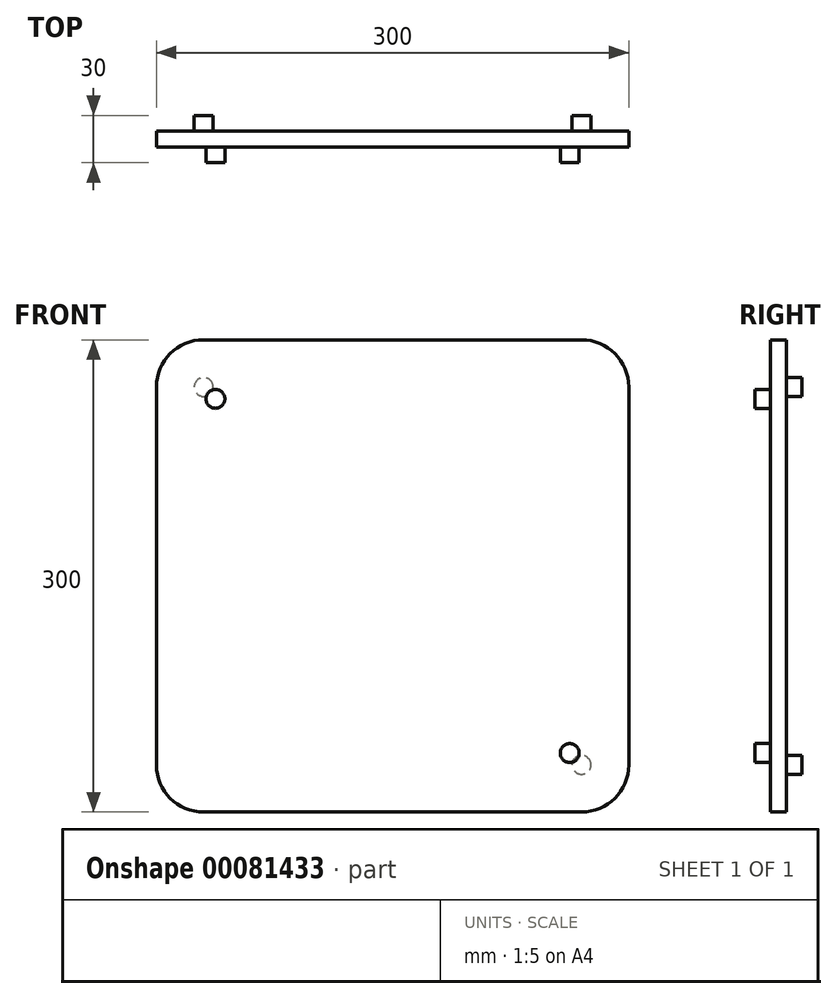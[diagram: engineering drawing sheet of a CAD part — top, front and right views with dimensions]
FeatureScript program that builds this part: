
annotation { "Feature Type Name" : "Feature", "Feature Type Description" : "" }
export const myFeature = defineFeature(function(context is Context, id is Id, definition is map)
    precondition{}
    {
        {
            var Q0;
            Q0=qCreatedBy(makeId("Front.planeOp"),FACE);
            var sketch = newSketch(context, id + "F0", { "sketchPlane" : qUnion([Q0])});
            skLineSegment(sketch, "E0.bottom", {"start": v(0, 0) * mm, "end": v(-300, 0) * mm});
            skLineSegment(sketch, "E0.top", {"start": v(0, 300) * mm, "end": v(-300, 300) * mm});
            skLineSegment(sketch, "E0.left", {"start": v(0, 0) * mm, "end": v(0, 300) * mm});
            skLineSegment(sketch, "E0.right", {"start": v(-300, 0) * mm, "end": v(-300, 300) * mm});
            skSolve(sketch);
        }
        {
            var Q0;
            Q0=makeQuery(id+"F0.imprint","IMPRINT",FACE,{"disambiguationData":[TD([[makeQuery(id+"F0.imprint","IMPRINT",EDGE,{"derivedFrom":sQuery(id+"F0.wireOp",EDGE,"E0.bottom")}),-1.0]])]});
            extrude(context, id + "F1", {"entities" : qUnion([Q0]), "depth" : 30 * mm});
        }
        {
            var Q0;
            Q0=makeQuery(id+"F1.opExtrude","SWEPT_EDGE",EDGE,{"disambiguationData":[OSD([sQuery(id+"F0.wireOp",EDGE,"E0.bottom"),sQuery(id+"F0.wireOp",EDGE,"E0.right")])]});
            var Q1;
            Q1=makeQuery(id+"F1.opExtrude","SWEPT_EDGE",EDGE,{"disambiguationData":[OSD([sQuery(id+"F0.wireOp",EDGE,"E0.bottom"),sQuery(id+"F0.wireOp",EDGE,"E0.left")])]});
            var Q2;
            Q2=makeQuery(id+"F1.opExtrude","SWEPT_EDGE",EDGE,{"disambiguationData":[OSD([sQuery(id+"F0.wireOp",EDGE,"E0.top"),sQuery(id+"F0.wireOp",EDGE,"E0.left")])]});
            var Q3;
            Q3=makeQuery(id+"F1.opExtrude","SWEPT_EDGE",EDGE,{"disambiguationData":[OSD([sQuery(id+"F0.wireOp",EDGE,"E0.top"),sQuery(id+"F0.wireOp",EDGE,"E0.right")])]});
            fillet(context, id + "F2", {"entities" : qUnion([Q0, Q1, Q2, Q3]), "radius" : 30 * mm, "tangentPropagation" : true, "allowEdgeOverflow" : false});
        }
        {
            var Q0;
            Q0=makeQuery(id+"F1.opExtrude","CAP_FACE",FACE,{"disambiguationData":[OSD([sQuery(id+"F0.wireOp",EDGE,"E0.bottom"),sQuery(id+"F0.wireOp",EDGE,"E0.top"),sQuery(id+"F0.wireOp",EDGE,"E0.left"),sQuery(id+"F0.wireOp",EDGE,"E0.right")])],"isStart":false});
            var sketch = newSketch(context, id + "F3", { "sketchPlane" : qUnion([Q0])});
            skLineSegment(sketch, "E1.0", {"start": v(-300, 30) * mm, "end": v(-300, 270) * mm});
            skLineSegment(sketch, "E1.1", {"start": v(-30, 300) * mm, "end": v(-270, 300) * mm});
            skLineSegment(sketch, "E1.2", {"start": v(-30, 0) * mm, "end": v(-270, 0) * mm});
            skLineSegment(sketch, "E1.3", {"start": v(0, 30) * mm, "end": v(0, 270) * mm});
            skArc(sketch, "E1.4", {"start": v(0, 270) * mm, "mid": v(-8.79, 291.21) * mm, "end": v(-30, 300) * mm});
            skArc(sketch, "E1.5", {"start": v(-270, 300) * mm, "mid": v(-291.21, 291.21) * mm, "end": v(-300, 270) * mm});
            skArc(sketch, "E1.6", {"start": v(-300, 30) * mm, "mid": v(-291.21, 8.79) * mm, "end": v(-270, 0) * mm});
            skArc(sketch, "E1.7", {"start": v(-30, 0) * mm, "mid": v(-8.79, 8.79) * mm, "end": v(0, 30) * mm});
            skLineSegment(sketch, "E1.8", {"start": v(-30, 300) * mm, "end": v(-270, 300) * mm});
            skLineSegment(sketch, "E2", {"start": v(-300, 150) * mm, "end": v(0, 150) * mm, "construction": true});
            skLineSegment(sketch, "E3", {"start": v(0, 150) * mm, "end": v(-150, 300) * mm, "construction": true});
            skLineSegment(sketch, "E4", {"start": v(-150, 300) * mm, "end": v(-150, 0) * mm, "construction": true});
            skCircle(sketch, "E5", {"center": v(-262.5, 37.5) * mm, "radius": 6 * mm});
            skCircle(sketch, "E6.MirrorC", {"center": v(-262.5, 262.5) * mm, "radius": 6 * mm});
            skCircle(sketch, "E7.MirrorC", {"center": v(-37.5, 37.5) * mm, "radius": 6 * mm});
            skCircle(sketch, "E8.MirrorC", {"center": v(-37.5, 262.5) * mm, "radius": 6 * mm});
            skSolve(sketch);
        }
        {
            var Q0;
            Q0=makeQuery(id+"F1.opExtrude","CAP_FACE",FACE,{"disambiguationData":[OSD([sQuery(id+"F0.wireOp",EDGE,"E0.bottom"),sQuery(id+"F0.wireOp",EDGE,"E0.top"),sQuery(id+"F0.wireOp",EDGE,"E0.left"),sQuery(id+"F0.wireOp",EDGE,"E0.right")])],"isStart":true});
            var sketch = newSketch(context, id + "F4", { "sketchPlane" : qUnion([Q0])});
            skLineSegment(sketch, "E9.0", {"start": v(300, 150) * mm, "end": v(0, 150) * mm, "construction": true});
            skLineSegment(sketch, "E9.1", {"start": v(0, 150) * mm, "end": v(150, 300) * mm, "construction": true});
            skLineSegment(sketch, "E9.2", {"start": v(150, 300) * mm, "end": v(150, 0) * mm, "construction": true});
            skLineSegment(sketch, "E9.3", {"start": v(0, 30) * mm, "end": v(0, 270) * mm});
            skLineSegment(sketch, "E9.4", {"start": v(300, 30) * mm, "end": v(300, 270) * mm});
            skLineSegment(sketch, "E9.5", {"start": v(30, 0) * mm, "end": v(270, 0) * mm});
            skLineSegment(sketch, "E9.6", {"start": v(30, 300) * mm, "end": v(270, 300) * mm});
            skCircle(sketch, "E10", {"center": v(270, 30) * mm, "radius": 6 * mm});
            skCircle(sketch, "E11.MirrorC", {"center": v(30, 30) * mm, "radius": 6 * mm});
            skCircle(sketch, "E12.MirrorC", {"center": v(30, 270) * mm, "radius": 6 * mm});
            skCircle(sketch, "E13.MirrorC", {"center": v(270, 270) * mm, "radius": 6 * mm});
            skSolve(sketch);
        }
        {
            var Q0;
            Q0=makeQuery(id+"F1.opExtrude","CAP_EDGE",EDGE,{"disambiguationData":[OSD([sQuery(id+"F0.wireOp",EDGE,"E0.right")])],"isStart":false});
            chamfer(context, id + "F5", {"entities" : qUnion([Q0]), "width" : 10 * mm, "tangentPropagation" : true});
        }
        {
            var Q0;
            Q0=makeQuery(id+"F3.imprint","IMPRINT",FACE,{"disambiguationData":[TD([[makeQuery(id+"F3.imprint","IMPRINT",EDGE,{"derivedFrom":sQuery(id+"F3.wireOp",EDGE,"E6.MirrorC")}),-1.0]])]});
            var Q1;
            Q1=makeQuery(id+"F3.imprint","IMPRINT",FACE,{"disambiguationData":[TD([[makeQuery(id+"F3.imprint","IMPRINT",EDGE,{"derivedFrom":sQuery(id+"F3.wireOp",EDGE,"E5")}),1.0]])]});
            var Q2;
            Q2=makeQuery(id+"F3.imprint","IMPRINT",FACE,{"disambiguationData":[TD([[makeQuery(id+"F3.imprint","IMPRINT",EDGE,{"derivedFrom":sQuery(id+"F3.wireOp",EDGE,"E7.MirrorC")}),-1.0]])]});
            var Q3;
            Q3=makeQuery(id+"F3.imprint","IMPRINT",FACE,{"disambiguationData":[TD([[makeQuery(id+"F3.imprint","IMPRINT",EDGE,{"derivedFrom":sQuery(id+"F3.wireOp",EDGE,"E8.MirrorC")}),1.0]])]});
            var Q4;
            Q4=makeQuery(id+"F4.imprint","IMPRINT",FACE,{"disambiguationData":[TD([[makeQuery(id+"F4.imprint","IMPRINT",EDGE,{"derivedFrom":sQuery(id+"F4.wireOp",EDGE,"E12.MirrorC")}),1.0]])]});
            var Q5;
            Q5=makeQuery(id+"F4.imprint","IMPRINT",FACE,{"disambiguationData":[TD([[makeQuery(id+"F4.imprint","IMPRINT",EDGE,{"derivedFrom":sQuery(id+"F4.wireOp",EDGE,"E13.MirrorC")}),-1.0]])]});
            var Q6;
            Q6=makeQuery(id+"F4.imprint","IMPRINT",FACE,{"disambiguationData":[TD([[makeQuery(id+"F4.imprint","IMPRINT",EDGE,{"derivedFrom":sQuery(id+"F4.wireOp",EDGE,"E10")}),1.0]])]});
            var Q7;
            Q7=makeQuery(id+"F4.imprint","IMPRINT",FACE,{"disambiguationData":[TD([[makeQuery(id+"F4.imprint","IMPRINT",EDGE,{"derivedFrom":sQuery(id+"F4.wireOp",EDGE,"E11.MirrorC")}),-1.0]])]});
            extrude(context, id + "F6", {"entities" : qUnion([Q0, Q1, Q2, Q3, Q4, Q5, Q6, Q7]), "operationType" : NewBodyOperationType.REMOVE, "oppositeDirection" : true, "depth" : 10 * mm});
        }
        {
            var Q0;
            Q0=makeQuery(id+"F4.imprint","IMPRINT",FACE,{"disambiguationData":[TD([[makeQuery(id+"F4.imprint","IMPRINT",EDGE,{"derivedFrom":sQuery(id+"F4.wireOp",EDGE,"E12.MirrorC")}),1.0]])]});
            var Q1;
            Q1=makeQuery(id+"F4.imprint","IMPRINT",FACE,{"disambiguationData":[TD([[makeQuery(id+"F4.imprint","IMPRINT",EDGE,{"derivedFrom":sQuery(id+"F4.wireOp",EDGE,"E13.MirrorC")}),-1.0]])]});
            var Q2;
            Q2=makeQuery(id+"F4.imprint","IMPRINT",FACE,{"disambiguationData":[TD([[makeQuery(id+"F4.imprint","IMPRINT",EDGE,{"derivedFrom":sQuery(id+"F4.wireOp",EDGE,"E10")}),1.0]])]});
            var Q3;
            Q3=makeQuery(id+"F4.imprint","IMPRINT",FACE,{"disambiguationData":[TD([[makeQuery(id+"F4.imprint","IMPRINT",EDGE,{"derivedFrom":sQuery(id+"F4.wireOp",EDGE,"E11.MirrorC")}),-1.0]])]});
            extrude(context, id + "F7", {"entities" : qUnion([Q0, Q1, Q2, Q3]), "operationType" : NewBodyOperationType.REMOVE, "oppositeDirection" : true, "depth" : 10 * mm});
        }
    });
